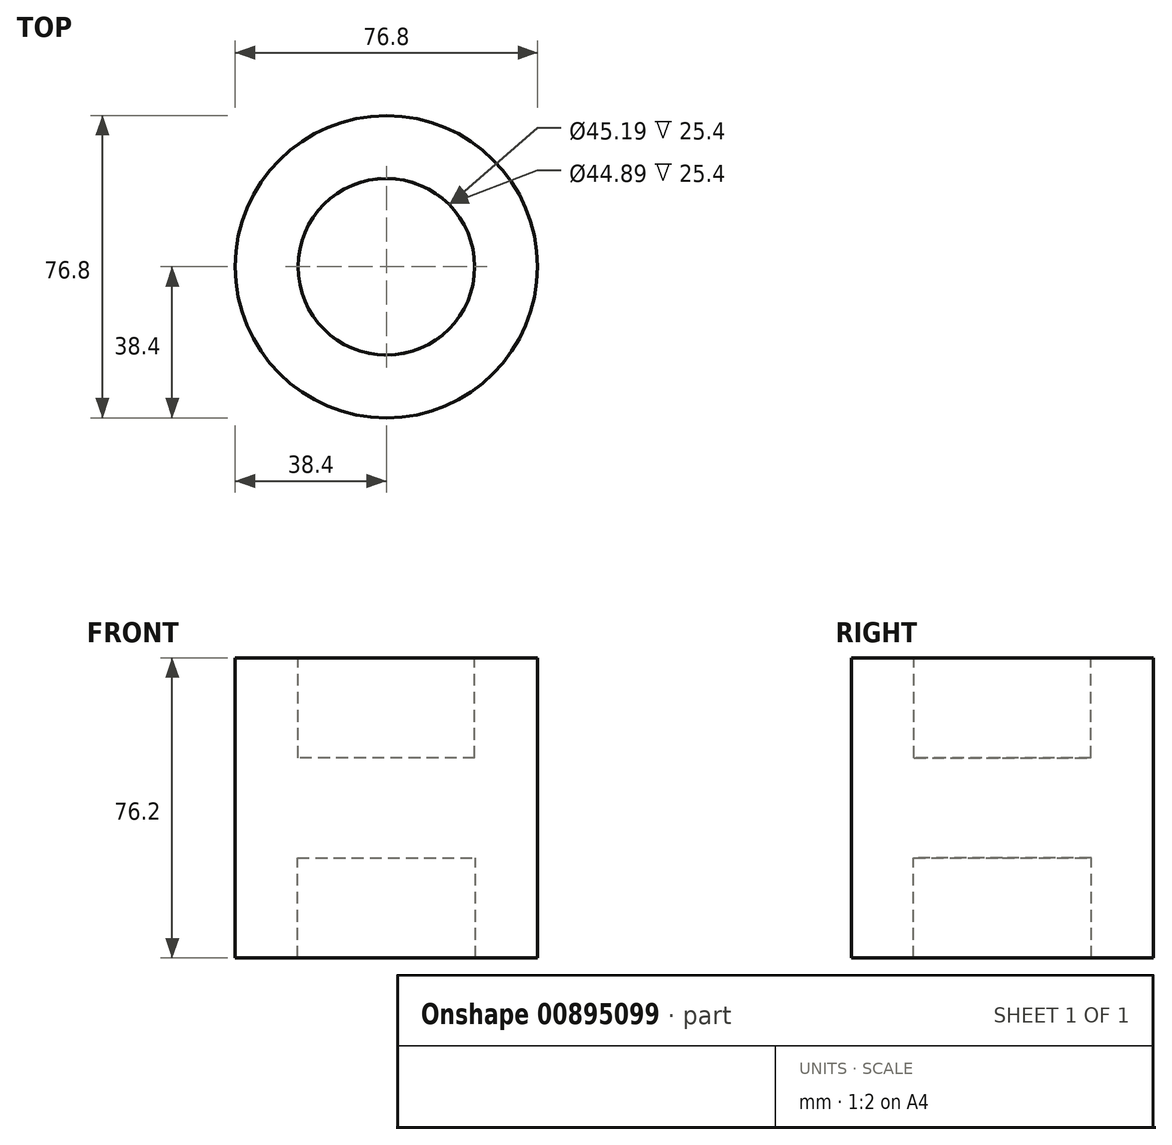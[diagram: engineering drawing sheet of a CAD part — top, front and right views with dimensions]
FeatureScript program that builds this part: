
annotation { "Feature Type Name" : "Feature", "Feature Type Description" : "" }
export const myFeature = defineFeature(function(context is Context, id is Id, definition is map)
    precondition{}
    {
        {
            var Q0;
            Q0=qCreatedBy(makeId("Top.planeOp"),FACE);
            var sketch = newSketch(context, id + "F0", { "sketchPlane" : qUnion([Q0])});
            skCircle(sketch, "E0", {"center": v(0, 0) * mm, "radius": 38.4 * mm});
            skSolve(sketch);
        }
        {
            var Q0;
            Q0=makeQuery(id+"F0.imprint","IMPRINT",FACE,{"disambiguationData":[TD([[makeQuery(id+"F0.imprint","IMPRINT",EDGE,{"derivedFrom":sQuery(id+"F0.wireOp",EDGE,"E0")}),1.0]])]});
            extrude(context, id + "F1", {"entities" : qUnion([Q0]), "endBound" : BoundingType.SYMMETRIC, "depth" : 76.2 * mm, "offsetDistance" : 25.4 * mm});
        }
        {
            var Q0;
            Q0=makeQuery(id+"F1.opExtrude","CAP_FACE",FACE,{"disambiguationData":[OSD([sQuery(id+"F0.wireOp",EDGE,"E0")])],"isStart":false});
            var sketch = newSketch(context, id + "F2", { "sketchPlane" : qUnion([Q0])});
            skCircle(sketch, "E1", {"center": v(0, 0) * mm, "radius": 22.44 * mm});
            skSolve(sketch);
        }
        {
            var Q0;
            Q0=makeQuery(id+"F1.opExtrude","CAP_FACE",FACE,{"disambiguationData":[OSD([sQuery(id+"F0.wireOp",EDGE,"E0")])],"isStart":true});
            var sketch = newSketch(context, id + "F3", { "sketchPlane" : qUnion([Q0])});
            skCircle(sketch, "E2", {"center": v(0, 0) * mm, "radius": 22.6 * mm});
            skSolve(sketch);
        }
        {
            var Q0;
            Q0=makeQuery(id+"F3.imprint","IMPRINT",FACE,{"disambiguationData":[TD([[makeQuery(id+"F3.imprint","IMPRINT",EDGE,{"derivedFrom":sQuery(id+"F3.wireOp",EDGE,"E2")}),1.0]])]});
            var Q1;
            Q1=makeQuery(id+"F2.imprint","IMPRINT",FACE,{"disambiguationData":[TD([[makeQuery(id+"F2.imprint","IMPRINT",EDGE,{"derivedFrom":sQuery(id+"F2.wireOp",EDGE,"E1")}),1.0]])]});
            extrude(context, id + "F4", {"entities" : qUnion([Q0, Q1]), "operationType" : NewBodyOperationType.REMOVE, "depth" : 25.4 * mm, "offsetDistance" : 25.4 * mm, "hasSecondDirection" : true, "secondDirectionOppositeDirection" : true, "secondDirectionDepth" : 25.4 * mm});
        }
    });
